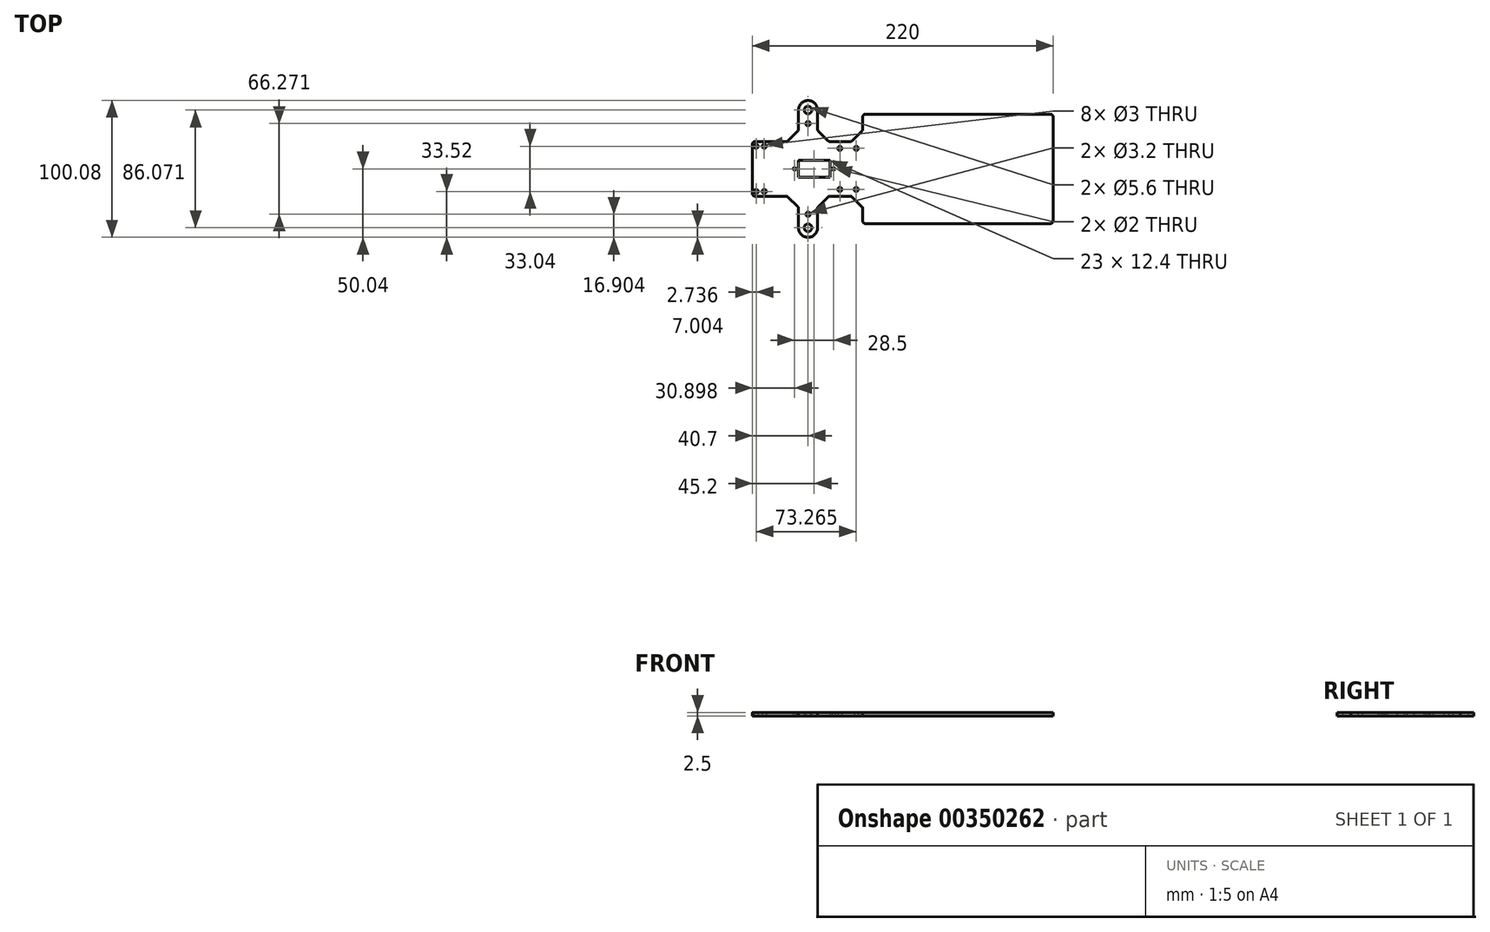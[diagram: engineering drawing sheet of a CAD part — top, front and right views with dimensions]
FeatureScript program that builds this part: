
annotation { "Feature Type Name" : "Feature", "Feature Type Description" : "" }
export const myFeature = defineFeature(function(context is Context, id is Id, definition is map)
    precondition{}
    {
        {
            var Q0;
            Q0=qCreatedBy(makeId("Top.planeOp"),FACE);
            var sketch = newSketch(context, id + "F0", { "sketchPlane" : qUnion([Q0])});
            skLineSegment(sketch, "E0", {"start": v(-75.77, 0) * mm, "end": v(152.01, 0) * mm, "construction": true});
            skLineSegment(sketch, "E1", {"start": v(-67.99, 0) * mm, "end": v(-67.99, 18) * mm});
            skLineSegment(sketch, "E2", {"start": v(-65.99, 20) * mm, "end": v(-43.22, 20) * mm});
            skLineSegment(sketch, "E3", {"start": v(-41.8, 20.59) * mm, "end": v(-34.29, 28.1) * mm});
            skLineSegment(sketch, "E4", {"start": v(-34.29, 28.1) * mm, "end": v(-34.29, 43.04) * mm});
            skLineSegment(sketch, "E5", {"start": v(-20.29, 43.04) * mm, "end": v(-20.29, 29.02) * mm});
            skLineSegment(sketch, "E6.0", {"start": v(-27.29, 43.04) * mm, "end": v(-27.29, -36.25) * mm, "construction": true});
            skArc(sketch, "E7", {"start": v(-20.29, 43.04) * mm, "mid": v(-27.29, 50.04) * mm, "end": v(-34.29, 43.04) * mm});
            skCircle(sketch, "E8", {"center": v(-27.29, 43.04) * mm, "radius": 2.8 * mm});
            skCircle(sketch, "E9", {"center": v(-27.29, 33.14) * mm, "radius": 1.6 * mm});
            skLineSegment(sketch, "E10", {"start": v(-19.7, 27.6) * mm, "end": v(-12.69, 20.59) * mm});
            skLineSegment(sketch, "E11", {"start": v(-11.27, 20) * mm, "end": v(3.7, 20) * mm});
            skLineSegment(sketch, "E12", {"start": v(12.71, 38) * mm, "end": v(12.71, 29.02) * mm});
            skLineSegment(sketch, "E13", {"start": v(12.12, 27.6) * mm, "end": v(5.1, 20.59) * mm});
            skLineSegment(sketch, "E14", {"start": v(14.71, 40) * mm, "end": v(150.01, 40) * mm});
            skLineSegment(sketch, "E15", {"start": v(152.01, 0) * mm, "end": v(152.01, 38) * mm});
            skLineSegment(sketch, "E16", {"start": v(-34.29, 6.2) * mm, "end": v(-34.29, 0) * mm});
            skLineSegment(sketch, "E17", {"start": v(-34.29, 6.2) * mm, "end": v(-11.29, 6.2) * mm});
            skLineSegment(sketch, "E18", {"start": v(-11.29, 6.2) * mm, "end": v(-11.29, 0) * mm});
            skCircle(sketch, "E19", {"center": v(-65.25, 16.52) * mm, "radius": 1.5 * mm});
            skCircle(sketch, "E20", {"center": v(-59.3, 16.52) * mm, "radius": 1.5 * mm});
            skCircle(sketch, "E21", {"center": v(-37.1, 0) * mm, "radius": 1 * mm});
            skCircle(sketch, "E22", {"center": v(-8.6, 0) * mm, "radius": 1 * mm});
            skCircle(sketch, "E23", {"center": v(-3.99, 15) * mm, "radius": 1.5 * mm});
            skCircle(sketch, "E24", {"center": v(8.01, 15) * mm, "radius": 1.5 * mm});
            skPoint(sketch, "E25.start.orphan", {"position": v(-27.29, 50.04) * mm});
            skLineSegment(sketch, "E26.MirrorCS", {"start": v(152.01, 0) * mm, "end": v(152.01, -38) * mm});
            skLineSegment(sketch, "E27.MirrorCS", {"start": v(14.71, -40) * mm, "end": v(150.01, -40) * mm});
            skLineSegment(sketch, "E28.MirrorCS", {"start": v(12.12, -27.6) * mm, "end": v(5.1, -20.59) * mm});
            skLineSegment(sketch, "E29.MirrorCS", {"start": v(-11.27, -20) * mm, "end": v(3.7, -20) * mm});
            skLineSegment(sketch, "E30.MirrorCS", {"start": v(-19.7, -27.6) * mm, "end": v(-12.69, -20.59) * mm});
            skLineSegment(sketch, "E31.MirrorCS", {"start": v(-20.29, -43.04) * mm, "end": v(-20.29, -29.02) * mm});
            skLineSegment(sketch, "E32.MirrorCS", {"start": v(12.71, -38) * mm, "end": v(12.71, -29.02) * mm});
            skArc(sketch, "E33.MirrorCS", {"start": v(-20.29, -43.04) * mm, "mid": v(-27.29, -50.04) * mm, "end": v(-34.29, -43.04) * mm});
            skCircle(sketch, "E34.MirrorC", {"center": v(-27.29, -43.04) * mm, "radius": 2.8 * mm});
            skCircle(sketch, "E35.MirrorC", {"center": v(-27.29, -33.14) * mm, "radius": 1.6 * mm});
            skCircle(sketch, "E36.MirrorC", {"center": v(-3.99, -15) * mm, "radius": 1.5 * mm});
            skCircle(sketch, "E37.MirrorC", {"center": v(8.01, -15) * mm, "radius": 1.5 * mm});
            skLineSegment(sketch, "E38.MirrorCS", {"start": v(-11.29, -6.2) * mm, "end": v(-11.29, 0) * mm});
            skLineSegment(sketch, "E39.MirrorCS", {"start": v(-34.29, -6.2) * mm, "end": v(-11.29, -6.2) * mm});
            skLineSegment(sketch, "E40.MirrorCS", {"start": v(-34.29, -6.2) * mm, "end": v(-34.29, 0) * mm});
            skCircle(sketch, "E41.MirrorC", {"center": v(-59.3, -16.52) * mm, "radius": 1.5 * mm});
            skCircle(sketch, "E42.MirrorC", {"center": v(-65.25, -16.52) * mm, "radius": 1.5 * mm});
            skLineSegment(sketch, "E43.MirrorCS", {"start": v(-67.99, 0) * mm, "end": v(-67.99, -18) * mm});
            skLineSegment(sketch, "E44.MirrorCS", {"start": v(-41.8, -20.59) * mm, "end": v(-34.88, -27.52) * mm});
            skLineSegment(sketch, "E45.MirrorCS", {"start": v(-34.29, -28.93) * mm, "end": v(-34.29, -43.04) * mm});
            skLineSegment(sketch, "E46.MirrorCS", {"start": v(-65.99, -20) * mm, "end": v(-43.22, -20) * mm});
            skPoint(sketch, "E47.visualSharp", {"position": v(-67.99, 20) * mm});
            skArc(sketch, "E47.filletArc", {"start": v(-65.99, 20) * mm, "mid": v(-67.4, 19.41) * mm, "end": v(-67.99, 18) * mm});
            skPoint(sketch, "E48.visualSharp", {"position": v(-67.99, -20) * mm});
            skArc(sketch, "E48.filletArc", {"start": v(-67.99, -18) * mm, "mid": v(-67.4, -19.41) * mm, "end": v(-65.99, -20) * mm});
            skPoint(sketch, "E49.visualSharp", {"position": v(12.71, 40) * mm});
            skArc(sketch, "E49.filletArc", {"start": v(14.71, 40) * mm, "mid": v(13.3, 39.41) * mm, "end": v(12.71, 38) * mm});
            skPoint(sketch, "E50.visualSharp", {"position": v(12.71, -40) * mm});
            skArc(sketch, "E50.filletArc", {"start": v(12.71, -38) * mm, "mid": v(13.3, -39.41) * mm, "end": v(14.71, -40) * mm});
            skPoint(sketch, "E51.visualSharp", {"position": v(152.01, -40) * mm});
            skArc(sketch, "E51.filletArc", {"start": v(150.01, -40) * mm, "mid": v(151.42, -39.41) * mm, "end": v(152.01, -38) * mm});
            skPoint(sketch, "E52.visualSharp", {"position": v(152.01, 40) * mm});
            skArc(sketch, "E52.filletArc", {"start": v(152.01, 38) * mm, "mid": v(151.42, 39.41) * mm, "end": v(150.01, 40) * mm});
            skPoint(sketch, "E53.visualSharp", {"position": v(12.71, 28.19) * mm});
            skArc(sketch, "E53.filletArc", {"start": v(12.12, 27.6) * mm, "mid": v(12.56, 28.25) * mm, "end": v(12.71, 29.02) * mm});
            skPoint(sketch, "E54.visualSharp", {"position": v(4.52, 20) * mm});
            skArc(sketch, "E54.filletArc", {"start": v(3.7, 20) * mm, "mid": v(4.46, 20.15) * mm, "end": v(5.1, 20.59) * mm});
            skPoint(sketch, "E55.visualSharp", {"position": v(-12.1, 20) * mm});
            skArc(sketch, "E55.filletArc", {"start": v(-12.69, 20.59) * mm, "mid": v(-12.04, 20.15) * mm, "end": v(-11.27, 20) * mm});
            skPoint(sketch, "E56.visualSharp", {"position": v(-20.29, 28.19) * mm});
            skArc(sketch, "E56.filletArc", {"start": v(-20.29, 29.02) * mm, "mid": v(-20.14, 28.25) * mm, "end": v(-19.7, 27.6) * mm});
            skPoint(sketch, "E57.visualSharp", {"position": v(-42.4, 20) * mm});
            skArc(sketch, "E57.filletArc", {"start": v(-43.22, 20) * mm, "mid": v(-42.46, 20.15) * mm, "end": v(-41.8, 20.59) * mm});
            skPoint(sketch, "E58.visualSharp", {"position": v(-42.4, -20) * mm});
            skArc(sketch, "E58.filletArc", {"start": v(-41.8, -20.59) * mm, "mid": v(-42.46, -20.15) * mm, "end": v(-43.22, -20) * mm});
            skPoint(sketch, "E59.visualSharp", {"position": v(-34.29, -28.1) * mm});
            skArc(sketch, "E59.filletArc", {"start": v(-34.29, -28.93) * mm, "mid": v(-34.44, -28.17) * mm, "end": v(-34.88, -27.52) * mm});
            skPoint(sketch, "E60.visualSharp", {"position": v(-20.29, -28.19) * mm});
            skArc(sketch, "E60.filletArc", {"start": v(-19.7, -27.6) * mm, "mid": v(-20.14, -28.25) * mm, "end": v(-20.29, -29.02) * mm});
            skPoint(sketch, "E61.visualSharp", {"position": v(-12.1, -20) * mm});
            skArc(sketch, "E61.filletArc", {"start": v(-11.27, -20) * mm, "mid": v(-12.04, -20.15) * mm, "end": v(-12.69, -20.59) * mm});
            skPoint(sketch, "E62.visualSharp", {"position": v(4.52, -20) * mm});
            skArc(sketch, "E62.filletArc", {"start": v(5.1, -20.59) * mm, "mid": v(4.46, -20.15) * mm, "end": v(3.7, -20) * mm});
            skPoint(sketch, "E63.visualSharp", {"position": v(12.71, -28.19) * mm});
            skArc(sketch, "E63.filletArc", {"start": v(12.71, -29.02) * mm, "mid": v(12.56, -28.25) * mm, "end": v(12.12, -27.6) * mm});
            skSolve(sketch);
        }
        {
            var Q0;
            Q0 = qSketchRegion(id + "F0", true);
            extrude(context, id + "F1", {"entities" : qUnion([Q0]), "endBound" : BoundingType.SYMMETRIC, "depth" : 2.5 * mm});
        }
    });
